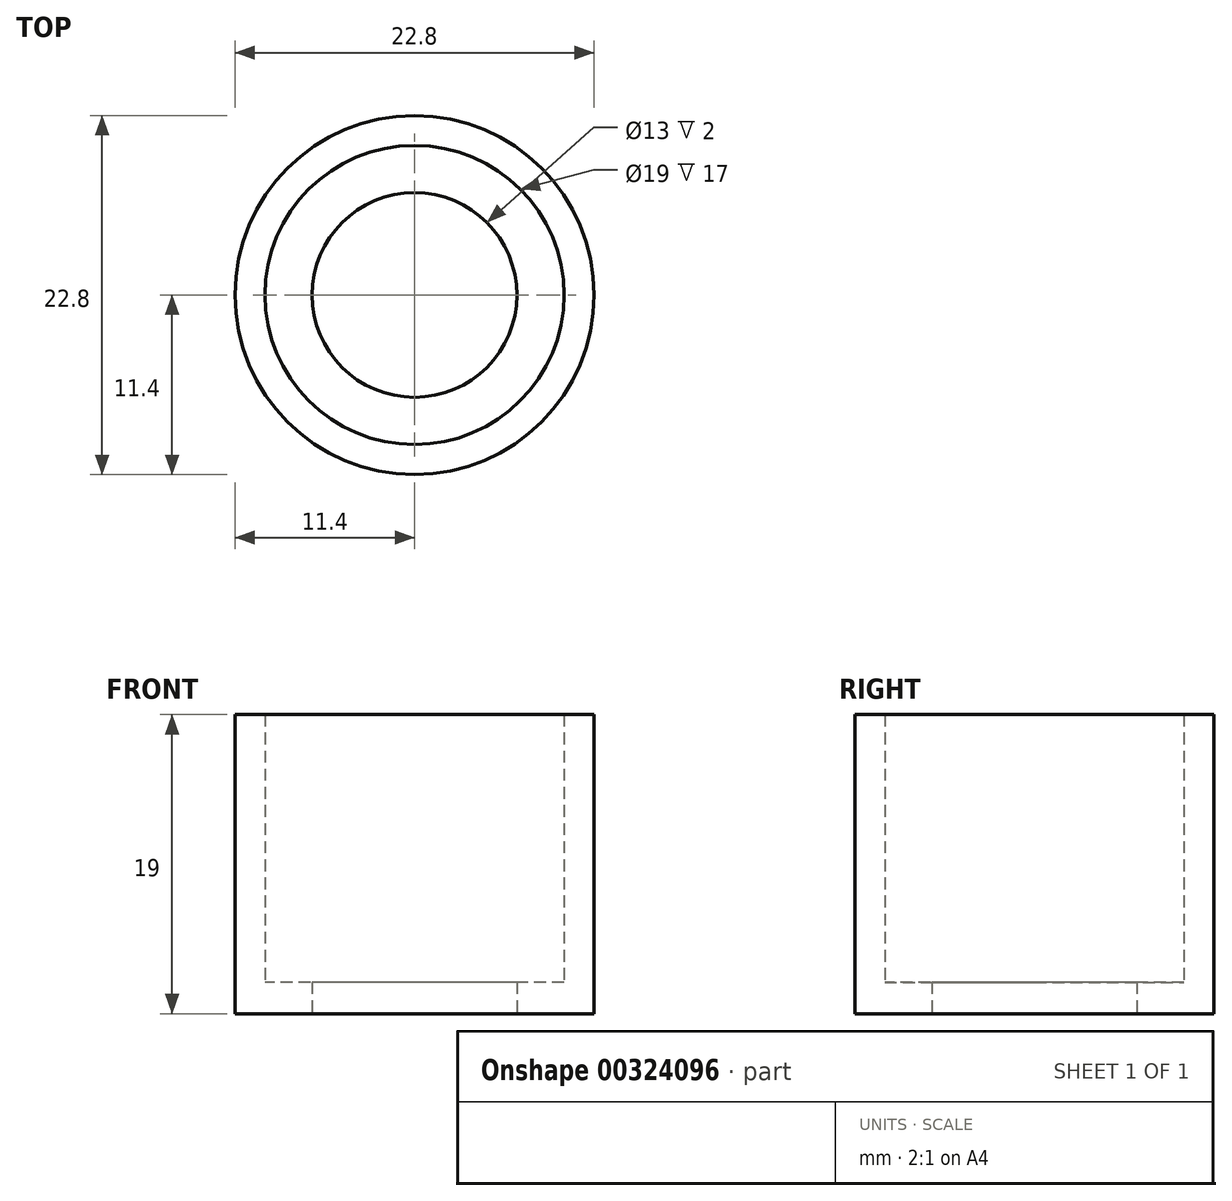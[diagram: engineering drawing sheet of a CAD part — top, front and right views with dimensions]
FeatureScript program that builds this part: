
annotation { "Feature Type Name" : "Feature", "Feature Type Description" : "" }
export const myFeature = defineFeature(function(context is Context, id is Id, definition is map)
    precondition{}
    {
        {
            var Q0;
            Q0=qCreatedBy(makeId("Top.planeOp"),FACE);
            var sketch = newSketch(context, id + "F0", { "sketchPlane" : qUnion([Q0])});
            skCircle(sketch, "E0", {"center": v(0, 0) * mm, "radius": 11.4 * mm});
            skCircle(sketch, "E1", {"center": v(0, 0) * mm, "radius": 9.5 * mm});
            skCircle(sketch, "E2", {"center": v(0, 0) * mm, "radius": 6.5 * mm});
            skSolve(sketch);
        }
        {
            var Q0;
            Q0=makeQuery(id+"F0.imprint","IMPRINT",FACE,{"disambiguationData":[TD([[makeQuery(id+"F0.imprint","IMPRINT",EDGE,{"derivedFrom":sQuery(id+"F0.wireOp",EDGE,"E0")}),1.0]])]});
            var Q1;
            Q1=makeQuery(id+"F0.imprint","IMPRINT",FACE,{"disambiguationData":[TD([[makeQuery(id+"F0.imprint","IMPRINT",EDGE,{"derivedFrom":sQuery(id+"F0.wireOp",EDGE,"E1")}),1.0]])]});
            extrude(context, id + "F1", {"entities" : qUnion([Q0, Q1]), "depth" : 2 * mm, "offsetDistance" : 25 * mm});
        }
        {
            var Q0;
            Q0=makeQuery(id+"F0.imprint","IMPRINT",FACE,{"disambiguationData":[TD([[makeQuery(id+"F0.imprint","IMPRINT",EDGE,{"derivedFrom":sQuery(id+"F0.wireOp",EDGE,"E0")}),1.0]])]});
            extrude(context, id + "F2", {"entities" : qUnion([Q0]), "operationType" : NewBodyOperationType.ADD, "depth" : 19 * mm, "offsetDistance" : 25 * mm});
        }
    });
